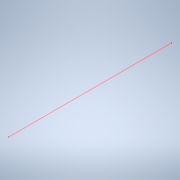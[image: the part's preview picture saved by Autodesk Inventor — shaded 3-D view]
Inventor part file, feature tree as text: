
AUTODESK INVENTOR PART (.ipt)
format: ipt  version: 2020 (Build 240168000, 168)  size: 100,864 bytes
history: native  units: mm
features: other x1, extrude x1, sketch x1
ambient origin geometry x8: Origin, YZ Plane, XZ Plane, XY Plane, X Axis, Y Axis, Z Axis, Center Point
bodies: Body1 (feature_tree)
feature tree (3):
  other  "솔리드1"
  extrude  "돌출1"  Depth=1.0mm
  sketch  "스케치1"
